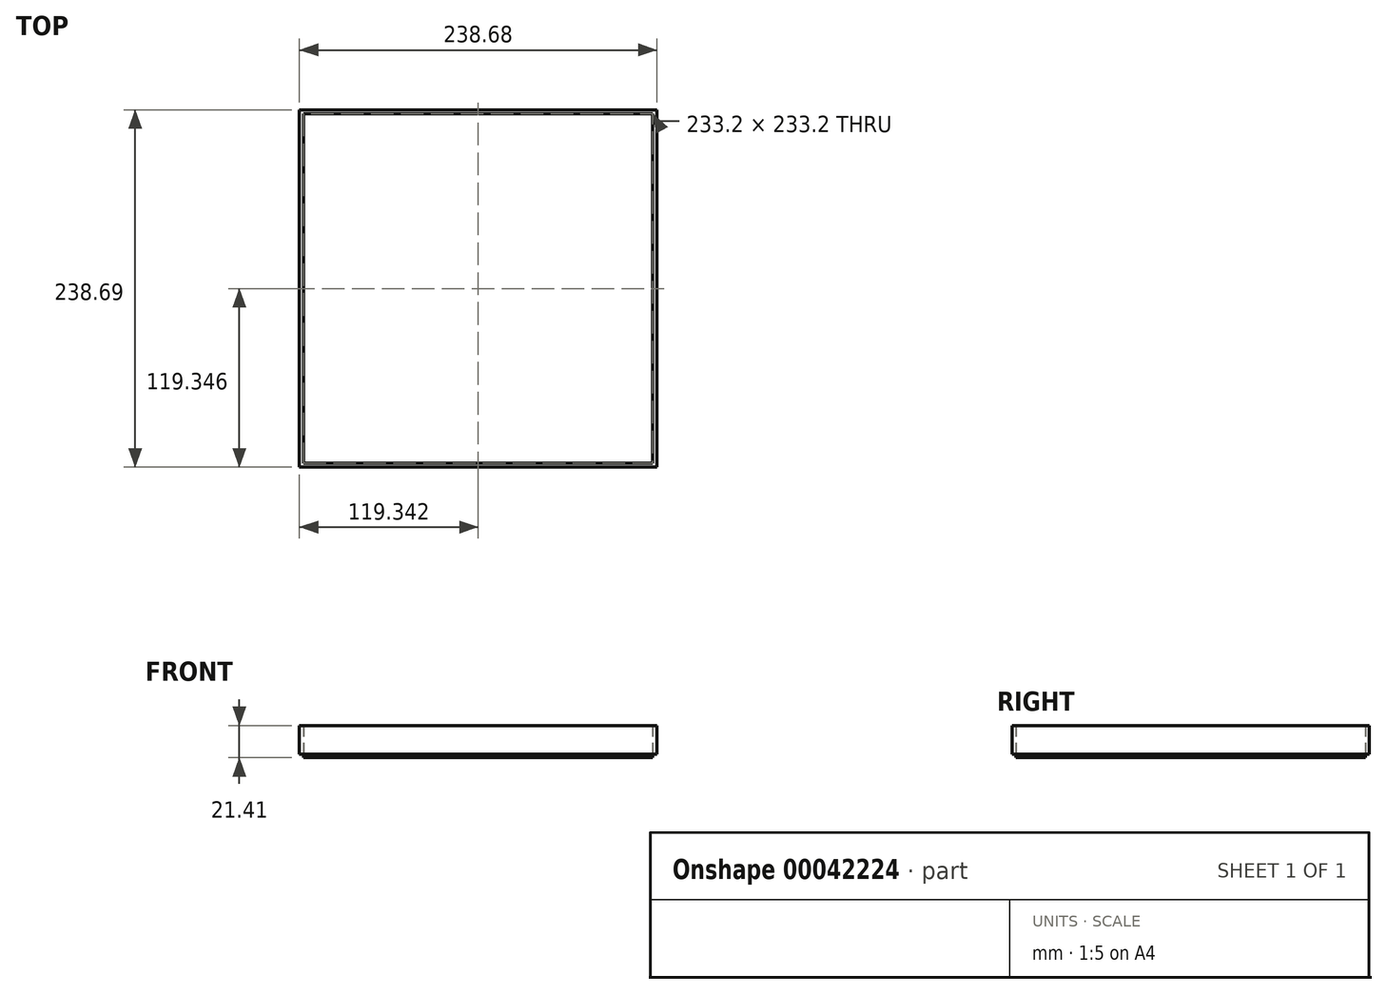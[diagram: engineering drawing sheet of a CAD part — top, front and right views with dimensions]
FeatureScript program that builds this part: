
annotation { "Feature Type Name" : "Feature", "Feature Type Description" : "" }
export const myFeature = defineFeature(function(context is Context, id is Id, definition is map)
    precondition{}
    {
        {
            var Q0;
            Q0=qCreatedBy(makeId("Top.planeOp"),FACE);
            var sketch = newSketch(context, id + "F0", { "sketchPlane" : qUnion([Q0])});
            skLineSegment(sketch, "E0.bottom", {"start": v(-178.9, 102.62) * mm, "end": v(54.3, 102.62) * mm});
            skLineSegment(sketch, "E0.top", {"start": v(-178.9, -130.58) * mm, "end": v(54.3, -130.58) * mm});
            skLineSegment(sketch, "E0.left", {"start": v(-178.9, 102.62) * mm, "end": v(-178.9, -130.58) * mm});
            skLineSegment(sketch, "E0.right", {"start": v(54.3, 102.62) * mm, "end": v(54.3, -130.58) * mm});
            skSolve(sketch);
        }
        {
            var Q0;
            Q0=makeQuery(id+"F0.imprint","IMPRINT",FACE,{"disambiguationData":[TD([[makeQuery(id+"F0.imprint","IMPRINT",EDGE,{"derivedFrom":sQuery(id+"F0.wireOp",EDGE,"E0.bottom")}),-1.0]])]});
            extrude(context, id + "F1", {"entities" : qUnion([Q0]), "depth" : 2.36 * mm});
        }
        {
            var Q0;
            Q0=makeQuery(id+"F1.opExtrude","CAP_FACE",FACE,{"disambiguationData":[OSD([sQuery(id+"F0.wireOp",EDGE,"E0.bottom"),sQuery(id+"F0.wireOp",EDGE,"E0.top"),sQuery(id+"F0.wireOp",EDGE,"E0.left"),sQuery(id+"F0.wireOp",EDGE,"E0.right")])],"isStart":false});
            var sketch = newSketch(context, id + "F2", { "sketchPlane" : qUnion([Q0])});
            skLineSegment(sketch, "E1.bottom", {"start": v(-181.65, 105.36) * mm, "end": v(57.03, 105.36) * mm});
            skLineSegment(sketch, "E1.top", {"start": v(-181.65, -133.33) * mm, "end": v(57.03, -133.33) * mm});
            skLineSegment(sketch, "E1.left", {"start": v(-181.65, 105.36) * mm, "end": v(-181.65, -133.33) * mm});
            skLineSegment(sketch, "E1.right", {"start": v(57.03, 105.36) * mm, "end": v(57.03, -133.33) * mm});
            skLineSegment(sketch, "E2", {"start": v(-178.9, -12.04) * mm, "end": v(-181.65, -12.04) * mm});
            skPoint(sketch, "E2.endSnap0", {"position": v(-181.65, -13.98) * mm});
            skLineSegment(sketch, "E3", {"start": v(-153.36, 105.36) * mm, "end": v(-153.36, 102.62) * mm});
            skLineSegment(sketch, "E4", {"start": v(54.3, -13.98) * mm, "end": v(57.03, -13.98) * mm});
            skLineSegment(sketch, "E5", {"start": v(-62.3, -130.58) * mm, "end": v(-62.3, -133.33) * mm});
            skPoint(sketch, "E5.startSnap0", {"position": v(-62.3, -133.33) * mm});
            skSolve(sketch);
        }
        {
            var Q0;
            {var subQ3=sQuery(id+"F2.wireOp",EDGE,"E2");Q0=makeQuery(id+"F2.imprint","IMPRINT",FACE,{"disambiguationData":[TD([[makeQuery(id+"F2.imprint","IMPRINT",EDGE,{"derivedFrom":subQ3}),-1.0]])]});}
            var Q1;
            {var subQ3=sQuery(id+"F2.wireOp",EDGE,"E2");Q1=makeQuery(id+"F2.imprint","IMPRINT",FACE,{"disambiguationData":[TD([[makeQuery(id+"F2.imprint","IMPRINT",EDGE,{"derivedFrom":subQ3}),1.0]])]});}
            var Q2;
            {var subQ7=sQuery(id+"F2.wireOp",EDGE,"E3");Q2=makeQuery(id+"F2.imprint","IMPRINT",FACE,{"disambiguationData":[TD([[makeQuery(id+"F2.imprint","IMPRINT",EDGE,{"derivedFrom":subQ7}),1.0]])]});}
            var Q3;
            {var subQ3=sQuery(id+"F2.wireOp",EDGE,"E4");Q3=makeQuery(id+"F2.imprint","IMPRINT",FACE,{"disambiguationData":[TD([[makeQuery(id+"F2.imprint","IMPRINT",EDGE,{"derivedFrom":subQ3}),-1.0]])]});}
            extrude(context, id + "F3", {"entities" : qUnion([Q0, Q1, Q2, Q3]), "depth" : 19.05 * mm});
        }
    });
